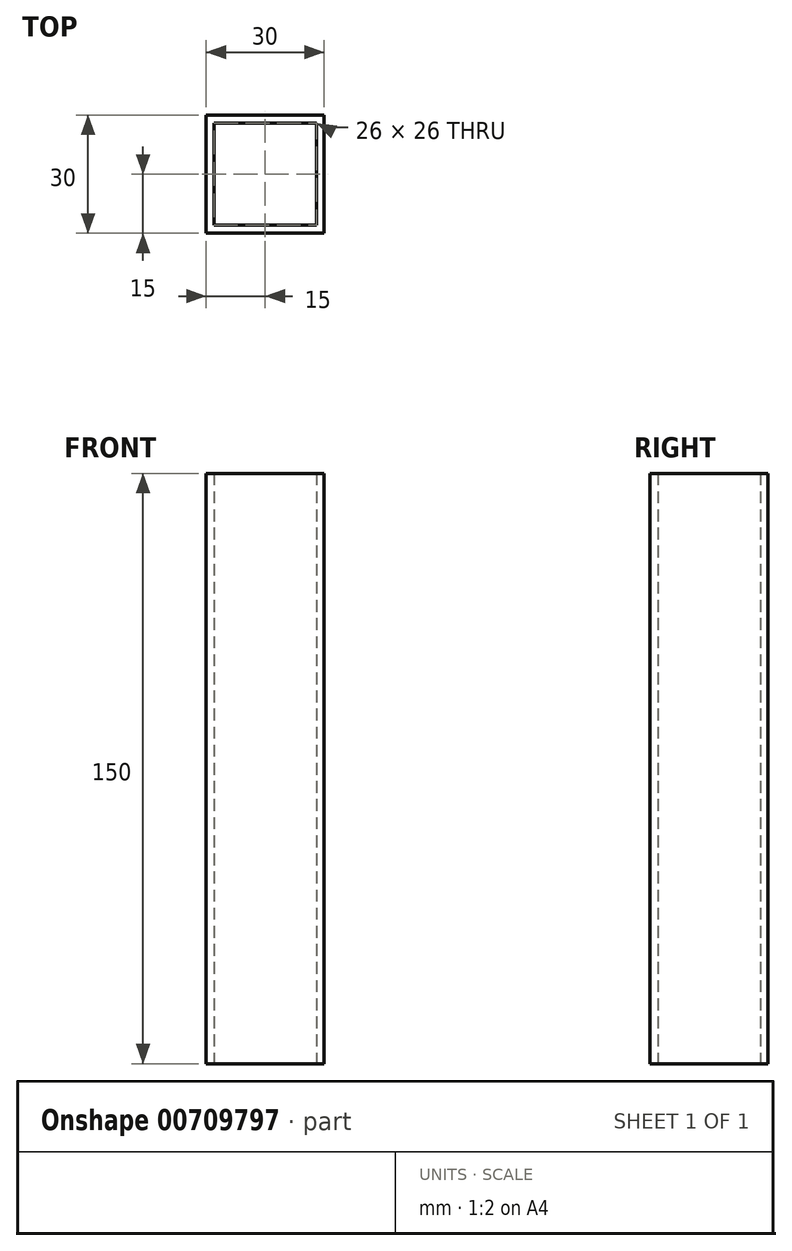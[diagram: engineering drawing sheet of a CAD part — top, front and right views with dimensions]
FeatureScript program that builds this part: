
annotation { "Feature Type Name" : "Feature", "Feature Type Description" : "" }
export const myFeature = defineFeature(function(context is Context, id is Id, definition is map)
    precondition{}
    {
        {
            var Q0;
            Q0=qCreatedBy(makeId("Top.planeOp"),FACE);
            var sketch = newSketch(context, id + "F0", { "sketchPlane" : qUnion([Q0])});
            skLineSegment(sketch, "E0.bottom", {"start": v(0, 0) * mm, "end": v(-30, 0) * mm});
            skLineSegment(sketch, "E0.top", {"start": v(0, -30) * mm, "end": v(-30, -30) * mm});
            skLineSegment(sketch, "E0.left", {"start": v(0, 0) * mm, "end": v(0, -30) * mm});
            skLineSegment(sketch, "E0.right", {"start": v(-30, 0) * mm, "end": v(-30, -30) * mm});
            skLineSegment(sketch, "E1.0", {"start": v(-28, -2) * mm, "end": v(-28, -28) * mm});
            skLineSegment(sketch, "E1.1", {"start": v(-2, -2) * mm, "end": v(-28, -2) * mm});
            skLineSegment(sketch, "E1.2", {"start": v(-2, -2) * mm, "end": v(-2, -28) * mm});
            skLineSegment(sketch, "E1.3", {"start": v(-2, -28) * mm, "end": v(-28, -28) * mm});
            skSolve(sketch);
        }
        {
            var Q0;
            Q0 = qSketchRegion(id + "F0", true);
            extrude(context, id + "F1", {"entities" : qUnion([Q0]), "depth" : 150 * mm, "offsetDistance" : 25 * mm});
        }
    });
